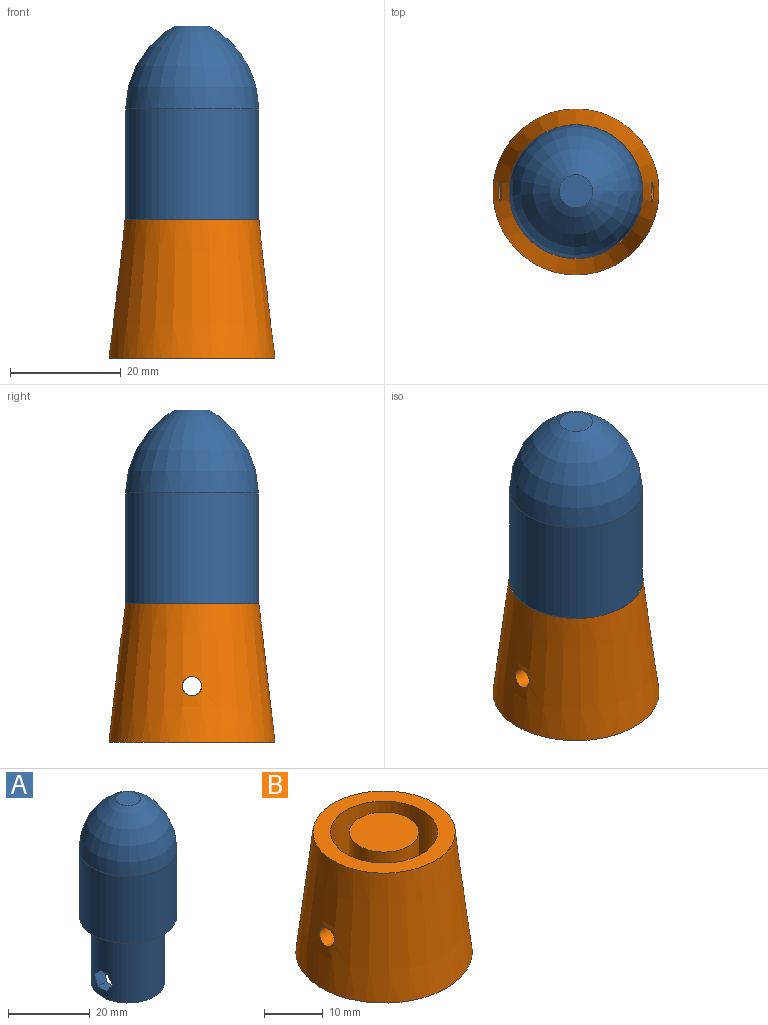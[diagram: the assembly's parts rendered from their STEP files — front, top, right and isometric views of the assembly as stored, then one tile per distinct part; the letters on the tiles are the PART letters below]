
ASSEMBLY  parts=2 mates=1
PART A: 20 faces, bbox 24x24x55 mm
  f0: cylinder r=6mm len=20mm, axis (0,0,1), area 702.5mm2, adj f6,f7,f8,f9,f10,f11,f12,f13
  f1: cylinder r=9mm len=20mm, axis (0,0,1), area 1080.4mm2, adj f3,f6,f8,f9,f10,f11,f12,f13
  f2: cylinder r=12mm len=24mm, axis (0,0,-1), area 1508mm2, adj f3,f5
  f3: plane 24x24mm, normal (0,0,-1), area 197.9mm2, adj f1,f2
  f4: plane 6x6mm, normal (0,0,1), area 28.3mm2, adj f5
  f5: revolved ~24x24mm, area 1025mm2, adj f2,f4
  f6: plane 18x18mm, normal (0,0,-1), area 141.4mm2, adj f0,f1
  f7: plane 12x12mm, normal (0,0,-1), area 113.1mm2, adj f0
  f8: plane 3.72x2.68mm, normal (0,0.87,-0.5), area 9.8mm2, adj f0,f1,f9,f13
  f9: plane 3.21x3.1mm, normal (0,0,-1), area 9.4mm2, adj f0,f1,f8,f10
  f10: plane 3.73x2.68mm, normal (0,-0.87,-0.5), area 9.8mm2, adj f0,f1,f9,f11
  f11: plane 3.73x2.68mm, normal (0,-0.87,0.5), area 9.8mm2, adj f0,f1,f10,f12
  f12: plane 3.21x3.1mm, normal (0,0,1), area 9.4mm2, adj f0,f1,f11,f13
  f13: plane 3.72x2.68mm, normal (0,0.87,0.5), area 9.8mm2, adj f0,f1,f8,f12
  f14: plane 3.72x2.68mm, normal (0,0.87,-0.5), area 9.8mm2, adj f0,f1,f15,f19
  f15: plane 3.21x3.1mm, normal (0,0,-1), area 9.4mm2, adj f0,f1,f14,f16
  f16: plane 3.73x2.68mm, normal (0,-0.87,-0.5), area 9.8mm2, adj f0,f1,f15,f17
  f17: plane 3.73x2.68mm, normal (0,-0.87,0.5), area 9.8mm2, adj f0,f1,f16,f18
  f18: plane 3.21x3.1mm, normal (0,0,1), area 9.4mm2, adj f0,f1,f17,f19
  f19: plane 3.72x2.68mm, normal (0,0.87,0.5), area 9.8mm2, adj f0,f1,f14,f18
PART B: 15 faces, bbox 30x30x25 mm
  f0: cylinder r=1.75mm len=4.05mm, axis (1,0,0), area 41mm2, adj f1,f11,f12,f13
  f1: cylinder r=5.9mm len=20mm, axis (0,0,1), area 721.9mm2, adj f0,f2,f7,f10
  f2: plane 11.8x11.8mm, normal (0,0,1), area 109.4mm2, adj f1
  f3: plane 30x30mm, normal (0,0,-1), area 687.3mm2, adj f4,f11,f13
  f4: cone r=15mm half-angle=6.6deg, axis (0,0,-1), area 2123.3mm2, adj f3,f5,f8,f9
  f5: plane 24.2x24.2mm, normal (0,0,1), area 199.8mm2, adj f4,f6
  f6: cylinder r=9.1mm len=20mm, axis (0,0,1), area 1124.1mm2, adj f5,f7,f8,f9
  f7: plane 18.2x18.2mm, normal (0,0,1), area 150.8mm2, adj f1,f6
  f8: cylinder r=1.75mm len=5.1mm, axis (1,0,0), area 52.3mm2, adj f4,f6
  f9: cylinder r=1.75mm len=5.1mm, axis (1,0,0), area 52.3mm2, adj f4,f6
  f10: cylinder r=1.75mm len=4.06mm, axis (1,0,0), area 39.1mm2, adj f1,f13
  f11: plane 9.12x2.89mm, normal (1,0,0), area 24.8mm2, adj f0,f3,f13
  f12: plane 2.89x1.94mm, normal (1,0,0), area 4mm2, adj f0,f13,f14
  f13: cylinder r=2.55mm len=13mm, axis (0,0,-1), area 156.9mm2, adj f0,f3,f10,f11,f12,f14
  f14: plane 5.1x4.65mm, normal (0,0,-1), area 19.5mm2, adj f12,f13
PLACE A at identity
PLACE B t=(0,0,0.09)mm
MATE fastened B.f1 <-> A.f0  axis (0,0,1) through (0,0,0)mm
